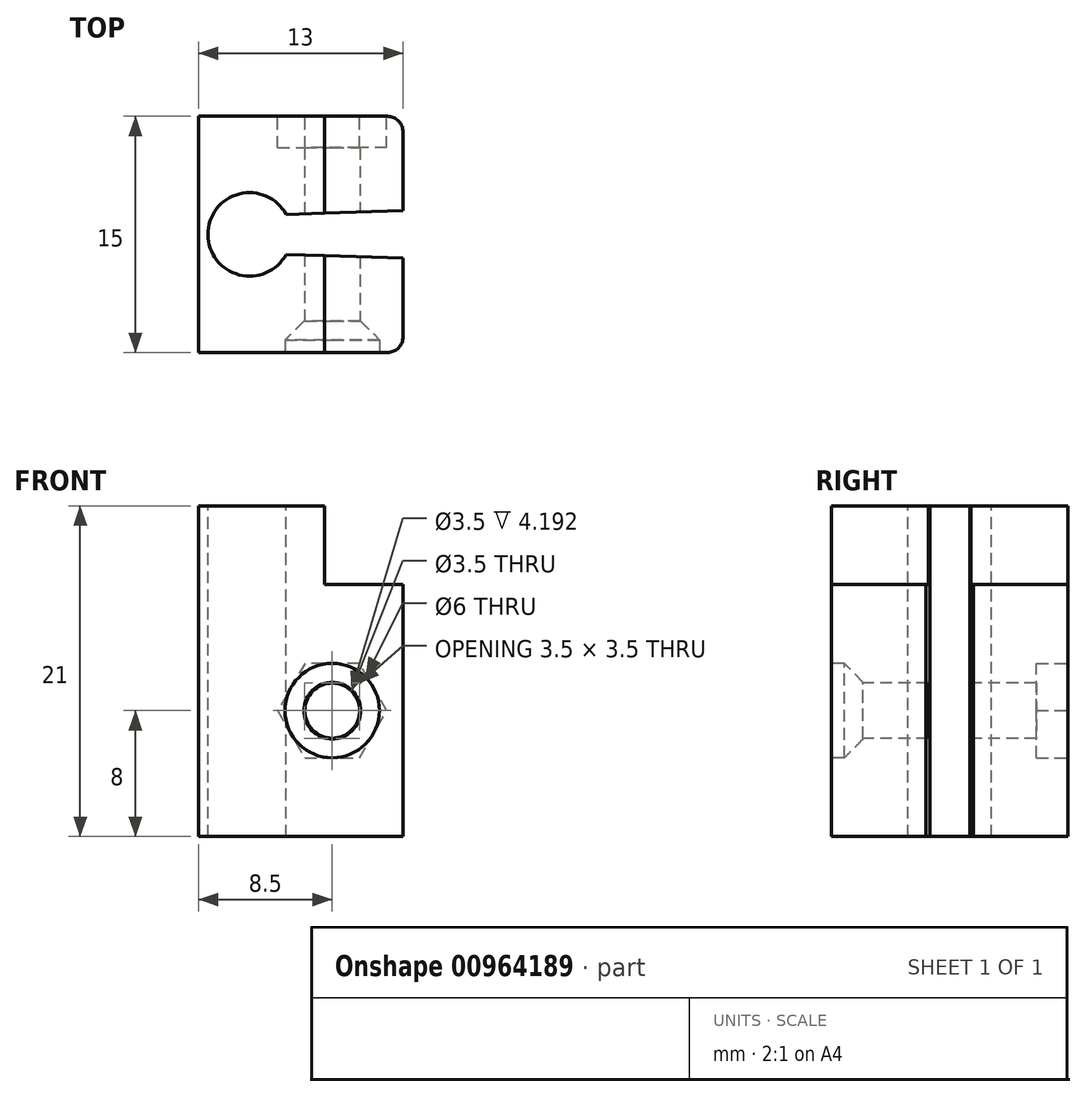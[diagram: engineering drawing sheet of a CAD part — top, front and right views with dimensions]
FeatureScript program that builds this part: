
annotation { "Feature Type Name" : "Feature", "Feature Type Description" : "" }
export const myFeature = defineFeature(function(context is Context, id is Id, definition is map)
    precondition{}
    {
        {
            var Q0;
            Q0=qCreatedBy(makeId("Top.planeOp"),FACE);
            var sketch = newSketch(context, id + "F0", { "sketchPlane" : qUnion([Q0])});
            skLineSegment(sketch, "E0.bottom", {"start": v(-6.5, 7.5) * mm, "end": v(6.5, 7.5) * mm});
            skLineSegment(sketch, "E0.top", {"start": v(-6.5, -7.5) * mm, "end": v(6.5, -7.5) * mm});
            skLineSegment(sketch, "E0.left", {"start": v(-6.5, 7.5) * mm, "end": v(-6.5, -7.5) * mm});
            skLineSegment(sketch, "E0.right", {"start": v(6.5, 7.5) * mm, "end": v(6.5, -7.5) * mm});
            skSolve(sketch);
        }
        {
            var Q0;
            Q0 = qSketchRegion(id + "F0", true);
            extrude(context, id + "F1", {"entities" : qUnion([Q0]), "depth" : 21 * mm, "offsetDistance" : 25 * mm});
        }
        {
            var Q0;
            Q0=makeQuery(id+"F1.opExtrude","CAP_FACE",FACE,{"disambiguationData":[OSD([sQuery(id+"F0.wireOp",EDGE,"E0.bottom"),sQuery(id+"F0.wireOp",EDGE,"E0.top"),sQuery(id+"F0.wireOp",EDGE,"E0.left"),sQuery(id+"F0.wireOp",EDGE,"E0.right")])],"isStart":false});
            var sketch = newSketch(context, id + "F2", { "sketchPlane" : qUnion([Q0])});
            skCircle(sketch, "E1", {"center": v(-3.25, 0) * mm, "radius": 2.65 * mm});
            skLineSegment(sketch, "E2.bottom", {"start": v(-0.93, 1.27) * mm, "end": v(6.5, 1.5) * mm});
            skLineSegment(sketch, "E2.top", {"start": v(-0.93, -1.27) * mm, "end": v(6.5, -1.5) * mm});
            skLineSegment(sketch, "E2.left", {"start": v(-0.93, 1.27) * mm, "end": v(-0.93, -1.27) * mm});
            skLineSegment(sketch, "E2.right", {"start": v(6.5, 1.5) * mm, "end": v(6.5, -1.5) * mm});
            skLineSegment(sketch, "E3", {"start": v(0, 0) * mm, "end": v(-3.25, 0) * mm, "construction": true});
            skLineSegment(sketch, "E4", {"start": v(-3.25, 0) * mm, "end": v(-6.5, 0) * mm, "construction": true});
            skSolve(sketch);
        }
        {
            var Q0;
            Q0 = qSketchRegion(id + "F2", true);
            extrude(context, id + "F3", {"entities" : qUnion([Q0]), "operationType" : NewBodyOperationType.REMOVE, "endBound" : BoundingType.UP_TO_NEXT, "oppositeDirection" : true, "depth" : 25 * mm, "offsetDistance" : 25 * mm});
        }
        {
            var Q0;
            Q0=makeQuery(id+"F1.opExtrude","CAP_FACE",FACE,{"disambiguationData":[OSD([sQuery(id+"F0.wireOp",EDGE,"E0.bottom"),sQuery(id+"F0.wireOp",EDGE,"E0.top"),sQuery(id+"F0.wireOp",EDGE,"E0.left"),sQuery(id+"F0.wireOp",EDGE,"E0.right")])],"isStart":false});
            var sketch = newSketch(context, id + "F4", { "sketchPlane" : qUnion([Q0])});
            skLineSegment(sketch, "E5.bottom", {"start": v(1.5, 7.5) * mm, "end": v(6.5, 7.5) * mm});
            skLineSegment(sketch, "E5.top", {"start": v(1.5, -7.5) * mm, "end": v(6.5, -7.5) * mm});
            skLineSegment(sketch, "E5.left", {"start": v(1.5, 7.5) * mm, "end": v(1.5, -7.5) * mm});
            skLineSegment(sketch, "E5.right", {"start": v(6.5, 7.5) * mm, "end": v(6.5, -7.5) * mm});
            skSolve(sketch);
        }
        {
            var Q0;
            Q0 = qSketchRegion(id + "F4", true);
            extrude(context, id + "F5", {"entities" : qUnion([Q0]), "operationType" : NewBodyOperationType.REMOVE, "oppositeDirection" : true, "depth" : 5 * mm, "offsetDistance" : 25 * mm});
        }
        {
            var Q0;
            Q0=makeQuery(id+"F4EAD4gJHIQlBfh_1.boolean.opBoolean","MERGE",FACE,{"derivedFrom":[makeQuery(id+"F1.opExtrude","SWEPT_FACE",FACE,{"disambiguationData":[OSD([sQuery(id+"F0.wireOp",EDGE,"E0.top")])]}),makeQuery(id+"F4EAD4gJHIQlBfh_1.opExtrude","SWEPT_FACE",FACE,{"disambiguationData":[OSD([sQuery(id+"FNnwEpf3wPBmdSt_1.wireOp",EDGE,"OW974nuk-RsTH-UiEq-BATl-WuunINrXE6Pl.top")])]})]});
            var sketch = newSketch(context, id + "F6", { "sketchPlane" : qUnion([Q0])});
            skCircle(sketch, "E6", {"center": v(2, 8) * mm, "radius": 1.75 * mm});
            skLineSegment(sketch, "E7", {"start": v(0, 16) * mm, "end": v(0, 0) * mm, "construction": true});
            skLineSegment(sketch, "E8", {"start": v(0, 8) * mm, "end": v(2, 8) * mm, "construction": true});
            skLineSegment(sketch, "E9", {"start": v(2, 8) * mm, "end": v(6.5, 8) * mm, "construction": true});
            skSolve(sketch);
        }
        {
            var Q0;
            Q0 = qSketchRegion(id + "F6", true);
            var Q1;
            Q1=makeQuery(id+"F4EAD4gJHIQlBfh_1.boolean.opBoolean","MERGE",FACE,{"derivedFrom":[makeQuery(id+"F1.opExtrude","SWEPT_FACE",FACE,{"disambiguationData":[OSD([sQuery(id+"F0.wireOp",EDGE,"E0.bottom")])]}),makeQuery(id+"F4EAD4gJHIQlBfh_1.opExtrude","SWEPT_FACE",FACE,{"disambiguationData":[OSD([sQuery(id+"FNnwEpf3wPBmdSt_1.wireOp",EDGE,"OW974nuk-RsTH-UiEq-BATl-WuunINrXE6Pl.bottom")])]})]});
            extrude(context, id + "F7", {"entities" : qUnion([Q0]), "operationType" : NewBodyOperationType.REMOVE, "endBound" : BoundingType.UP_TO_SURFACE, "oppositeDirection" : true, "depth" : 25 * mm, "endBoundEntityFace" : qUnion([Q1]), "offsetDistance" : 25 * mm});
        }
        {
            var Q0;
            Q0=makeQuery(id+"F4EAD4gJHIQlBfh_1.boolean.opBoolean","MERGE",FACE,{"derivedFrom":[makeQuery(id+"F1.opExtrude","SWEPT_FACE",FACE,{"disambiguationData":[OSD([sQuery(id+"F0.wireOp",EDGE,"E0.bottom")])]}),makeQuery(id+"F4EAD4gJHIQlBfh_1.opExtrude","SWEPT_FACE",FACE,{"disambiguationData":[OSD([sQuery(id+"FNnwEpf3wPBmdSt_1.wireOp",EDGE,"OW974nuk-RsTH-UiEq-BATl-WuunINrXE6Pl.bottom")])]})]});
            var sketch = newSketch(context, id + "F8", { "sketchPlane" : qUnion([Q0])});
            skCircle(sketch, "E10.0", {"center": v(-2, 8) * mm, "radius": 1.75 * mm});
            skCircle(sketch, "E11.cCircle", {"center": v(-2, 8) * mm, "radius": 3 * mm, "construction": true});
            skLineSegment(sketch, "E11.0", {"start": v(-3.73, 11) * mm, "end": v(-0.27, 11) * mm});
            skLineSegment(sketch, "E11.1", {"start": v(-0.27, 11) * mm, "end": v(1.46, 8) * mm});
            skLineSegment(sketch, "E11.2", {"start": v(1.46, 8) * mm, "end": v(-0.27, 5) * mm});
            skLineSegment(sketch, "E11.3", {"start": v(-0.27, 5) * mm, "end": v(-3.73, 5) * mm});
            skLineSegment(sketch, "E11.4", {"start": v(-3.73, 5) * mm, "end": v(-5.46, 8) * mm});
            skLineSegment(sketch, "E11.5", {"start": v(-5.46, 8) * mm, "end": v(-3.73, 11) * mm});
            skPoint(sketch, "E11.0.midPoint", {"position": v(-2, 11) * mm});
            skSolve(sketch);
        }
        {
            var Q0;
            Q0 = qSketchRegion(id + "F8", true);
            extrude(context, id + "F9", {"entities" : qUnion([Q0]), "operationType" : NewBodyOperationType.REMOVE, "oppositeDirection" : true, "depth" : 2 * mm, "offsetDistance" : 25 * mm});
        }
        {
            var Q0;
            Q0=makeQuery(id+"F4EAD4gJHIQlBfh_1.boolean.opBoolean","MERGE",FACE,{"derivedFrom":[makeQuery(id+"F1.opExtrude","SWEPT_FACE",FACE,{"disambiguationData":[OSD([sQuery(id+"F0.wireOp",EDGE,"E0.top")])]}),makeQuery(id+"F4EAD4gJHIQlBfh_1.opExtrude","SWEPT_FACE",FACE,{"disambiguationData":[OSD([sQuery(id+"FNnwEpf3wPBmdSt_1.wireOp",EDGE,"OW974nuk-RsTH-UiEq-BATl-WuunINrXE6Pl.top")])]})]});
            var sketch = newSketch(context, id + "F10", { "sketchPlane" : qUnion([Q0])});
            skCircle(sketch, "E12.0", {"center": v(2, 8) * mm, "radius": 1.75 * mm});
            skCircle(sketch, "E13", {"center": v(2, 8) * mm, "radius": 3 * mm});
            skSolve(sketch);
        }
        {
            var Q0;
            Q0 = qSketchRegion(id + "F10", true);
            extrude(context, id + "F11", {"entities" : qUnion([Q0]), "operationType" : NewBodyOperationType.REMOVE, "oppositeDirection" : true, "depth" : 2 * mm, "offsetDistance" : 25 * mm});
        }
        {
            var Q0;
            Q0=makeQuery(id+"F11.boolean.opBoolean","COPY",EDGE,{"derivedFrom":makeQuery(id+"F11.opExtrude","CAP_EDGE",EDGE,{"disambiguationData":[OSD([sQuery(id+"F10.wireOp",EDGE,"E13")])],"isStart":false})});
            chamfer(context, id + "F12", {"entities" : qUnion([Q0]), "width" : 1.2 * mm, "tangentPropagation" : true});
        }
        {
            var Q0;
            Q0=makeQuery(id+"F1.opExtrude","SWEPT_EDGE",EDGE,{"disambiguationData":[OSD([sQuery(id+"F0.wireOp",EDGE,"E0.top"),sQuery(id+"F0.wireOp",EDGE,"E0.right")])]});
            var Q1;
            Q1=makeQuery(id+"F1.opExtrude","SWEPT_EDGE",EDGE,{"disambiguationData":[OSD([sQuery(id+"F0.wireOp",EDGE,"E0.bottom"),sQuery(id+"F0.wireOp",EDGE,"E0.right")])]});
            fillet(context, id + "F13", {"entities" : qUnion([Q0, Q1]), "radius" : 1 * mm, "tangentPropagation" : true, "allowEdgeOverflow" : false});
        }
    });
